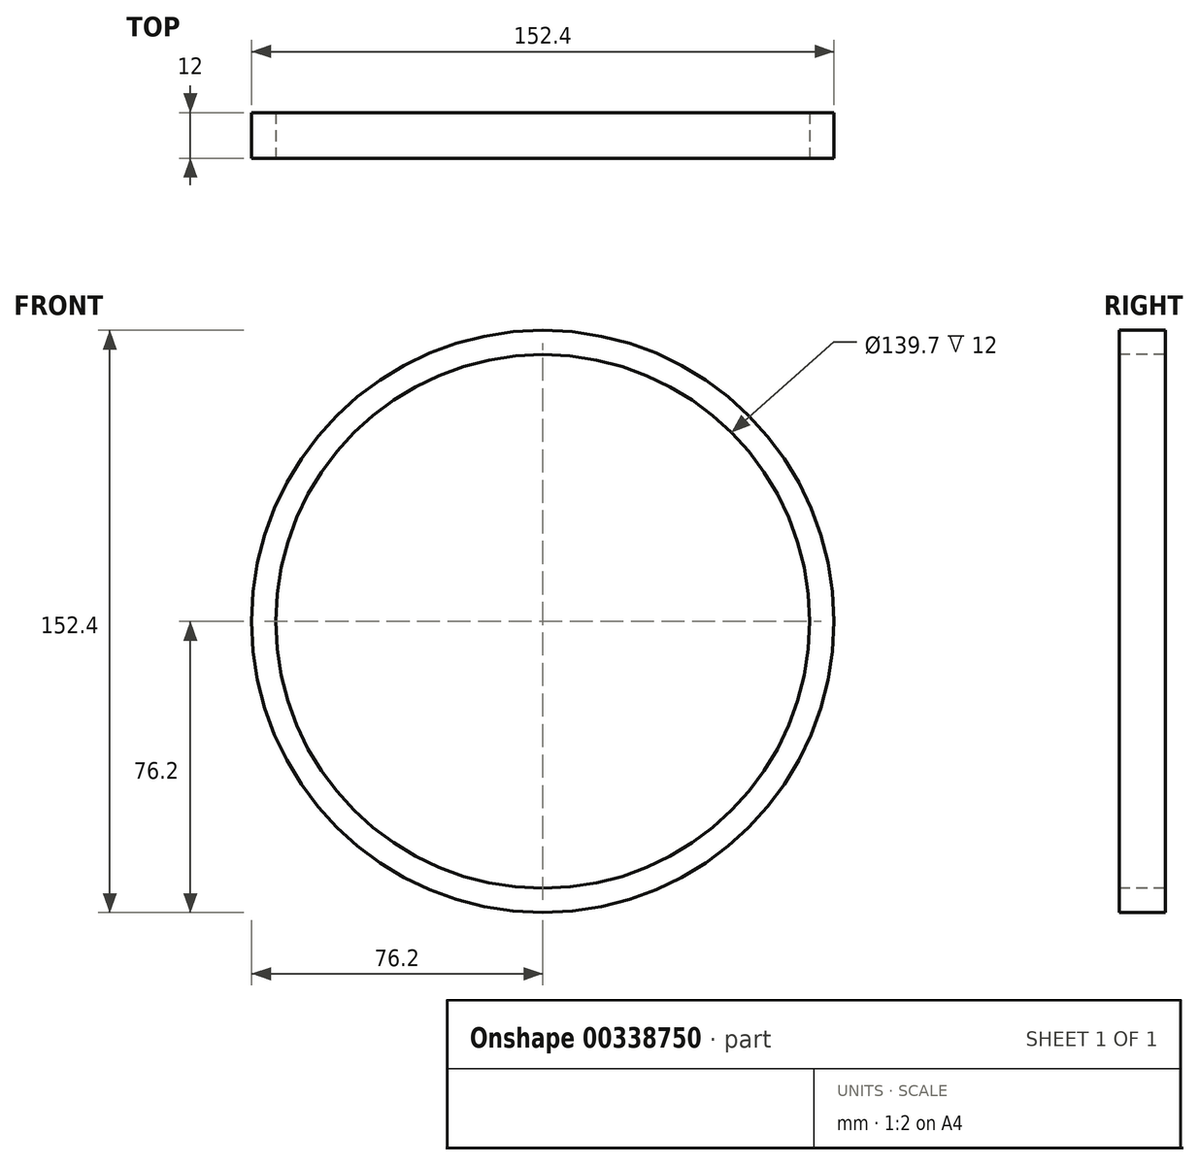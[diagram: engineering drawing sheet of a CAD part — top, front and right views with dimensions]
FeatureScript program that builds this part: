
annotation { "Feature Type Name" : "Feature", "Feature Type Description" : "" }
export const myFeature = defineFeature(function(context is Context, id is Id, definition is map)
    precondition{}
    {
        {
            assignVariable(context, id + "F0", {"name" : "Length", "anyValue" : 12});
        }
        {
            var Q0;
            Q0=qCreatedBy(makeId("Front.planeOp"),FACE);
            var sketch = newSketch(context, id + "F1", { "sketchPlane" : qUnion([Q0])});
            skCircle(sketch, "E0", {"center": v(0, 0) * mm, "radius": 76.2 * mm});
            skSolve(sketch);
        }
        {
            var Q0;
            Q0=qSketchRegion(id+"F1",true);
            extrude(context, id + "F2", {"entities" : qUnion([Q0]), "oppositeDirection" : true, "depth" : (getVariable(context, 'Length')) * mm});
        }
        {
            var Q0;
            Q0=makeQuery(id+"F2.opExtrude","CAP_FACE",FACE,{"disambiguationData":[OSD([sQuery(id+"F1.wireOp",EDGE,"E0")])],"isStart":true});
            var Q1;
            Q1=makeQuery(id+"F2.opExtrude","CAP_FACE",FACE,{"disambiguationData":[OSD([sQuery(id+"F1.wireOp",EDGE,"E0")])],"isStart":false});
            shell(context, id + "F3", {"entities" : qUnion([Q0, Q1]), "thickness" : 6.35 * mm});
        }
    });
